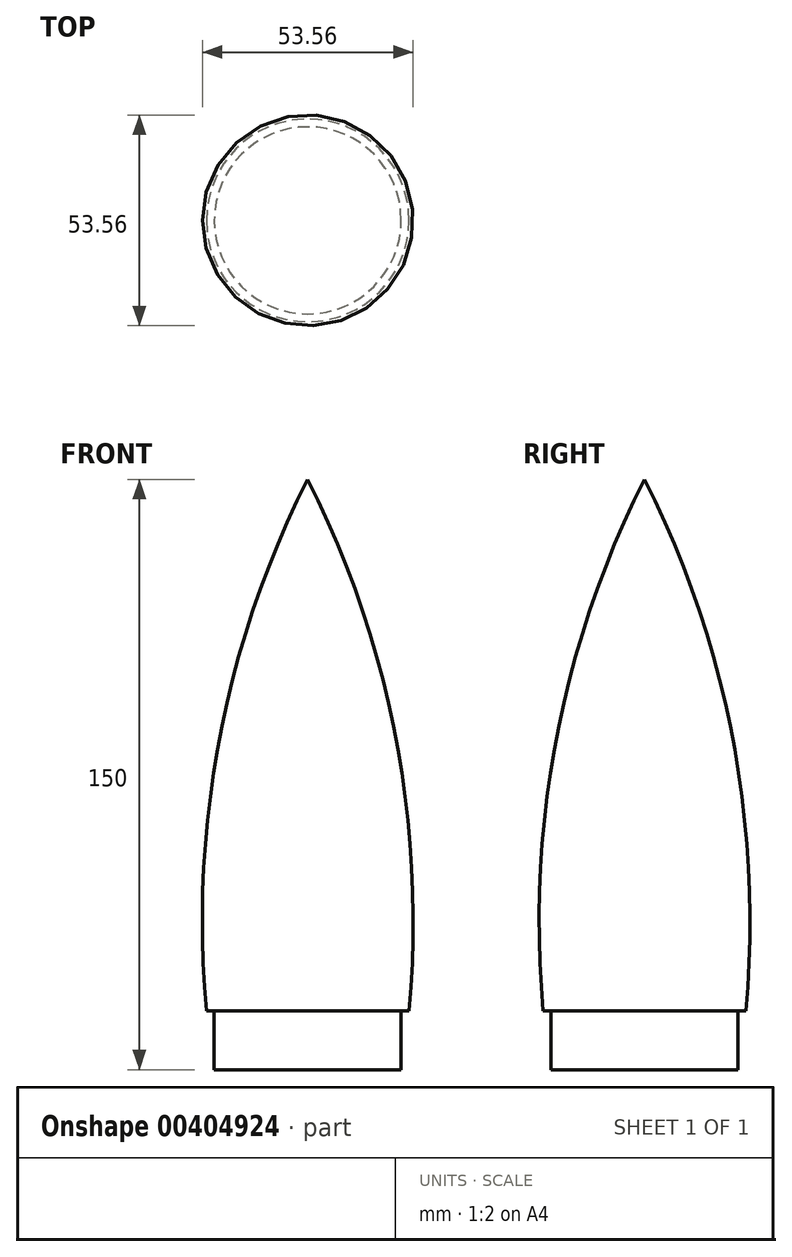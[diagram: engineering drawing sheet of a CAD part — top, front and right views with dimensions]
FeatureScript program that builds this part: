
annotation { "Feature Type Name" : "Feature", "Feature Type Description" : "" }
export const myFeature = defineFeature(function(context is Context, id is Id, definition is map)
    precondition{}
    {
        {
            var Q0;
            Q0=qCreatedBy(makeId("Front.planeOp"),FACE);
            var sketch = newSketch(context, id + "F0", { "sketchPlane" : qUnion([Q0])});
            skLineSegment(sketch, "E0", {"start": v(0, 0) * mm, "end": v(25.75, 0) * mm});
            skLineSegment(sketch, "E1", {"start": v(0, -15) * mm, "end": v(23.75, -15) * mm});
            skLineSegment(sketch, "E2", {"start": v(0, 135) * mm, "end": v(0, -15) * mm});
            skLineSegment(sketch, "E3", {"start": v(23.75, -15) * mm, "end": v(23.75, 0) * mm});
            skArc(sketch, "E4", {"start": v(25.75, 0) * mm, "mid": v(22.37, 69.31) * mm, "end": v(0, 135) * mm});
            skSolve(sketch);
        }
        {
            var Q0;
            {var subQ4=sQuery(id+"F0.wireOp",EDGE,"E4");Q0=makeQuery(id+"F0.imprint","IMPRINT",FACE,{"disambiguationData":[TD([[makeQuery(id+"F0.imprint","IMPRINT",EDGE,{"derivedFrom":subQ4}),1.0]])]});}
            var Q1;
            {var subQ4=sQuery(id+"F0.wireOp",EDGE,"E1");Q1=makeQuery(id+"F0.imprint","IMPRINT",FACE,{"disambiguationData":[TD([[makeQuery(id+"F0.imprint","IMPRINT",EDGE,{"derivedFrom":subQ4}),1.0]])]});}
            var Q2;
            Q2=sQuery(id+"F0.wireOp",EDGE,"E2");
            revolve(context, id + "F1", {"entities" : qUnion([Q0, Q1]), "axis" : qUnion([Q2]), "revolveType" : RevolveType.FULL});
        }
    });
